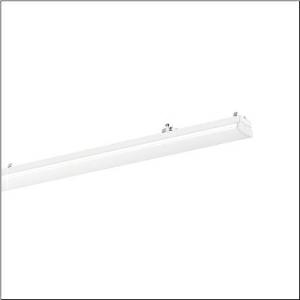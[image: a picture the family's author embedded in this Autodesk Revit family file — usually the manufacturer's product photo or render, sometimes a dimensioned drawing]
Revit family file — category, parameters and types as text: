
# Revit family: licross_r__21_recessed_opal_mo_52te1d7n48xg_0b46
name_source: partatom
category: Lighting Fixtures
units: mm (PartAtom-declared; Revit-internal decimal feet)

## family parameters
Cut with Voids When Loaded = No
Host = Face
Light Source = No
Part Type = Normal
Room Calculation Point = No
Round Connector Dimension = Use Diameter
Shared = No

## types (1)
- Licross® 21 recessed opal MO (1 x LED, 8360 lm, 47.9 W, 4000K)
    Apparent Load = 48 VA
    CIE Flux Codes = 44 73 91 87 100
    Color Rendering = 80
    Color Temperature = 4000K
    Default Elevation = 1800 mm
    Description = Licross® 21 recessed opal MO, luminaire insert, of sheet steel, galvanised, coil coated, white, length: 1.500mm, width: 66mm, height: 67mm, LED rated luminous flux: 8.360lm, light colour: 840, control gear: ON/OFF, with plug, 3-pole, with phase selection, mains connection: 220..240V, AC, 50/60Hz, rated input power: 48W, internal wiring halogen-free, primary optical cover: cover, of PMMA, light emission: direct with ceiling illumination distribution, primary light characteristic: symmetric, protection rating (complete): IP54, insulation class (complete): insulation class I (protective earthing), certification: CE, ENEC, VDE, UKCA, protection symbol: D if used in an environment with non-conductive dust loads with corresponding accessories, impact resistance: IK06, permissible ambient temperature for indoor applications: -35..+40°C, corresponds to IFS (International Featured Standards) requirements for safety and quality in the food industry, reducing of maximum allowable ambient temperature of 5°C with ceiling mounting, LABS conformity tested according to VDMA 24364:2018-05, packaging unit: 1 piece
    Height = 83 mm
    Lamp = 1 x LED
    Lamp Light Flux = 8360 lm
    Lamp Power = 47.9 W
    Lamp count = 1
    Length = 1500 mm
    Luminous efficacy = 175 lm/W
    Manufacturer = Siteco
    ModVariant = No
    Model = 52TE1D7N48XG
    Mounting Place = Ceiling
    Mounting Type = Pendant
    Number of Poles = 1
    OnlyDefault = Yes
    Power Factor = 1
    Product Name = Licross® 21 recessed opal MO
    Product group = luminaire insert | ceiling pendant
    ProductGroupID = 902
    Protection Class = Protection class I
    Protection Degree = IP 54
    RLX_Detail_Level = 1
    RLX_Emergency_Light_Flux = 0 lm
    RLX_Emergency_Type = 0
    RLX_Emergency_Type_DB = No
    RlxData = <blob elided: 23149 chars, md5=c0a8a884>
    Socket = socket
    Standby Power = 0 W
    System Light Flux = 8360 lm
    System Power = 48 W
    Type Comments = Product without accessories
    Type Image = l_1313666.jpg
    URL = http://relux.com
    VarID = ---
    Voltage = 0 V
    Weight = 0.00 kg
    Width = 76 mm

## geometry (parser evidence)
native form markers: Blend x4, Sweep x15
no freeform markers — native parametric forms only
